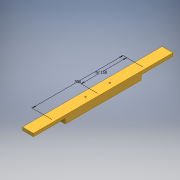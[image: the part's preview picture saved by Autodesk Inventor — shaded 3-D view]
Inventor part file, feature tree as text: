
AUTODESK INVENTOR PART (.ipt)
format: ipt  version: 2016 (Build 200138000, 138)  size: 141,824 bytes
history: native  units: mm
features: sketch x5, extrude x3, hole x1
ambient origin geometry x8: Origin, YZ Plane, XZ Plane, XY Plane, X Axis, Y Axis, Z Axis, Center Point
bodies: Solid1 (feature_tree)
feature tree (9):
  sketch  "Sketch1"  dims[d0=16.0mm d1=111.075mm]
  sketch  "Sketch2"  dims[d2=55.5375mm d3=8.0mm]
  sketch  "Sketch3"  dims[d4=80.0mm d5=40.0mm]
  extrude  "baseExtrusion"  Depth=16.0mm
  hole  "xyStageAttach_m5"  [1 undecoded]
  extrude  "Extrusion2"  Depth=40.0mm
  extrude  "Extrusion3"  Depth=10.0mm
  sketch  "Sketch4"  dims[d6=10.0mm d7=174.4253mm]
  sketch  "Sketch5"  dims[d8=10.0mm d9=174.4253mm d10=300.0mm d11=150.0mm d12=10.0mm d13=0.0mm d14=4.134mm d15=10.0mm d16=4.0mm d17=2.0mm d18=90.0deg d19=14.2mm d20=20.594885mm d28=125.0mm d29=125.0mm d30=16.0mm d31=0.0mm d32=150.0mm d33=75.0mm d34=20.0mm d35=10.0mm d36=16.0mm d37=0.0mm]
note: 1 required parameter value undecoded (feature->parameter linkage not recoverable at this tier; creation-order binding heuristic only, values carry confidence <= 0.55)
